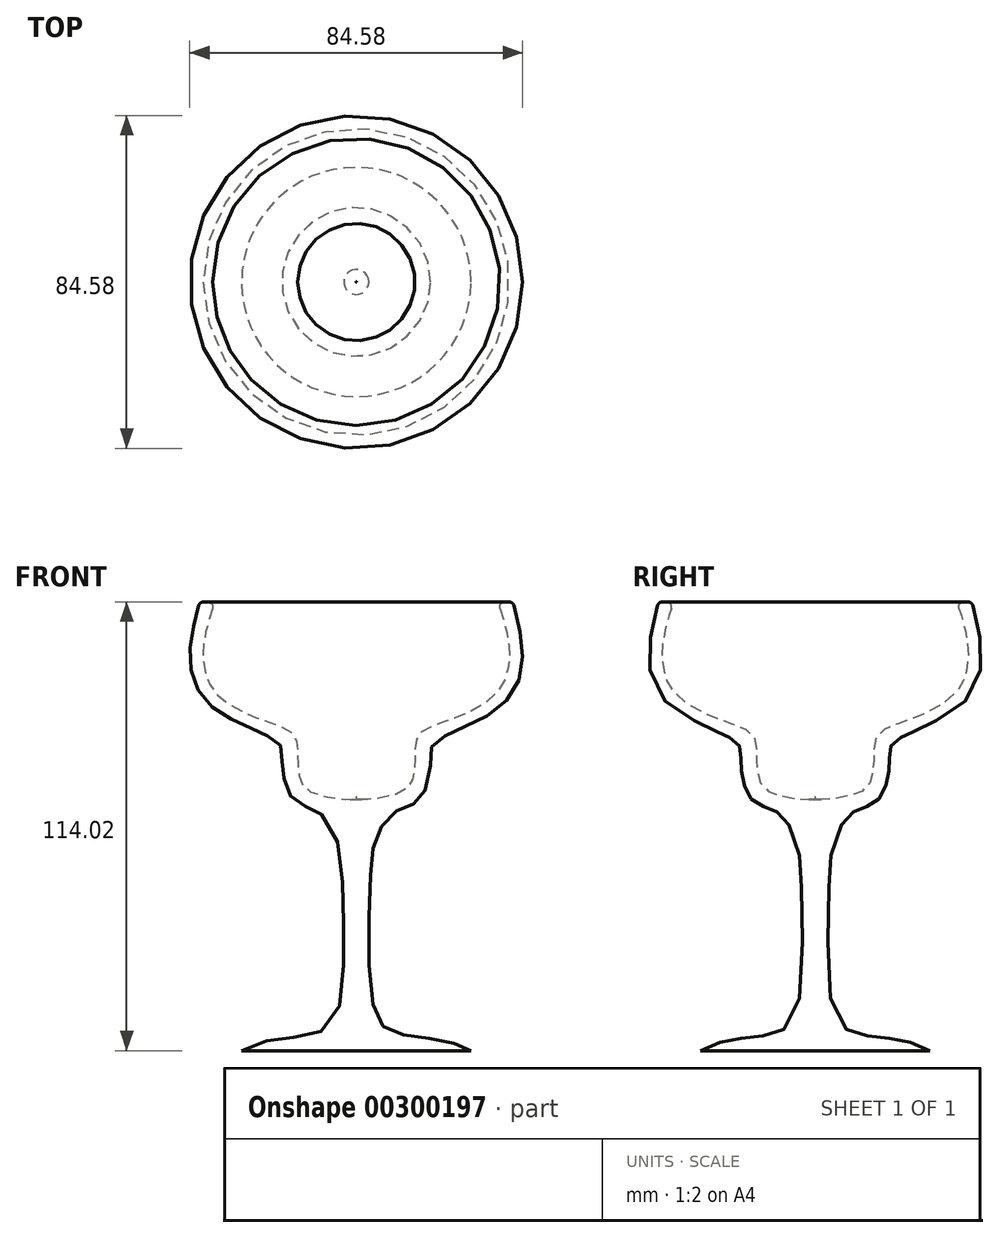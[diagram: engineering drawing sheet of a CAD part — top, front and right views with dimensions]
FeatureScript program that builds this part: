
annotation { "Feature Type Name" : "Feature", "Feature Type Description" : "" }
export const myFeature = defineFeature(function(context is Context, id is Id, definition is map)
    precondition{}
    {
        {
            var Q0;
            Q0=qCreatedBy(makeId("Front.planeOp"),FACE);
            var sketch = newSketch(context, id + "F0", { "sketchPlane" : qUnion([Q0])});
            skLineSegment(sketch, "E0", {"start": v(0, 76.45) * mm, "end": v(0, -76) * mm, "construction": true});
            skLineSegment(sketch, "E1", {"start": v(-39.78, 56) * mm, "end": v(-36, 56) * mm});
            skFitSpline(sketch, "E2", {"points": [v(-39.78, 56) * mm, v(-42, 46) * mm, v(-41.78, 37.78) * mm, v(-37.78, 30.45) * mm, v(-30.23, 25.56) * mm, v(-23.56, 22.45) * mm, v(-19.34, 19.56) * mm, v(-18.9, 15.11) * mm, v(-16.9, 6.89) * mm, v(-13.56, 4.22) * mm, v(-8.9, 2) * mm, v(-4.89, -4.45) * mm, v(-3.56, -14.67) * mm, v(-3.78, -43.56) * mm, v(-7.33, -52.23) * mm, v(-14.9, -54.45) * mm, v(-24.45, -56) * mm, v(-29.11, -58) * mm, v(-29.56, -58) * mm], "startDerivative": vector(-41.42, -157.9) * mm, "endDerivative": vector(-25.75, 6.03) * mm});
            skLineSegment(sketch, "E3", {"start": v(-29.11, -58) * mm, "end": v(0, -58) * mm});
            skLineSegment(sketch, "E4", {"start": v(0, -58) * mm, "end": v(0, 6.45) * mm});
            skFitSpline(sketch, "E5", {"points": [v(-36, 56) * mm, v(-38, 49.34) * mm, v(-38.9, 43.56) * mm, v(-38.45, 38.67) * mm, v(-36.45, 33.78) * mm, v(-29.56, 28.45) * mm, v(-20, 24.67) * mm, v(-15.56, 21.78) * mm, v(-14.9, 16.45) * mm, v(-14.22, 10.9) * mm, v(-10.67, 7.33) * mm, v(0, 6) * mm, v(0, 6.45) * mm], "startDerivative": vector(-24, -73.76) * mm, "endDerivative": vector(-10.33, 21.4) * mm});
            skPoint(sketch, "E6.orphan", {"position": v(0, 56) * mm});
            skSolve(sketch);
        }
        {
            var Q0;
            Q0 = qSketchRegion(id + "F0", true);
            var Q1;
            Q1=sQuery(id+"F0.wireOp",EDGE,"E0");
            revolve(context, id + "F1", {"entities" : qUnion([Q0]), "axis" : qUnion([Q1]), "revolveType" : RevolveType.FULL});
        }
        {
            var Q0;
            Q0=makeQuery(id+"F1.opRevolve","SWEPT_EDGE",EDGE,{"disambiguationData":[OSD([sQuery(id+"F0.wireOp",EDGE,"E1"),sQuery(id+"F0.wireOp",EDGE,"E2")])]});
            var Q1;
            Q1=makeQuery(id+"F1.opRevolve","SWEPT_EDGE",EDGE,{"disambiguationData":[OSD([sQuery(id+"F0.wireOp",EDGE,"E1"),sQuery(id+"F0.wireOp",EDGE,"E5")])]});
            fillet(context, id + "F2", {"entities" : qUnion([Q0, Q1]), "radius" : 1.27 * mm, "tangentPropagation" : true, "allowEdgeOverflow" : false});
        }
    });
